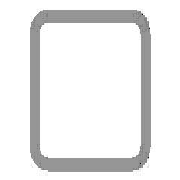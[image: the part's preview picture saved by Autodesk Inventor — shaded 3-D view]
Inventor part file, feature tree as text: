
AUTODESK INVENTOR PART (.ipt)
format: ipt  version: 2024 (Build 280153000, 153)  size: 140,288 bytes
history: native  units: mm (DEFAULTED — no unit token found)
features: other x4, plane x2, extrude x1, split x1, sketch x1
ambient origin geometry x8: Origin, YZ Plane, XZ Plane, XY Plane, X Axis, Y Axis, Z Axis, Center Point
bodies: Solid1 (feature_tree)
feature tree (9):
  parser-record x1  (decoder bookkeeping rows leaked as tree rows — omitted from the tree; the rows remain in map.json)
  other  "Driven Length"
  other  "Plano inicial"
  other  "Plano final"
  extrude  "Cuerpo"  TaperAngle=0.0deg  [1 undecoded]
  plane  "Plano de trabajo4"
  split  "Dividir1"
  sketch  "Sketch3"  dims[d3=525.4mm d4=0.0mm d10=50.8mm d11=50.8mm d12=3.175mm d13=-0.0mm d14=525.4mm d15=25.4mm d16=25.4mm d17=6.35mm d18=90.0deg d19=525.4mm]
  plane  "Work Plane3"
note: 1 required parameter value undecoded (feature->parameter linkage not recoverable at this tier; creation-order binding heuristic only, values carry confidence <= 0.55)
